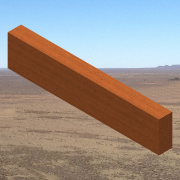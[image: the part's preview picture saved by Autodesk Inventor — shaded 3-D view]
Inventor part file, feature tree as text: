
AUTODESK INVENTOR PART (.ipt)
format: ipt  version: 2014 SP1 (Build 180222100, 222)  size: 126,976 bytes
history: native  units: in
note: dims shown in document units (in); Inventor stores cm internally (conversion verified against a paired STEP export)
features: extrude x1, sketch x1
ambient origin geometry x8: Origin, YZ Plane, XZ Plane, XY Plane, X Axis, Y Axis, Z Axis, Center Point
bodies: Solid1 (feature_tree)
feature tree (2):
  extrude  "Extrusion1"  Depth=3.5in
  sketch  "Sketch1"  dims[d0=1.5in d1=3.5in d2=17.0in d3=0.0in]
